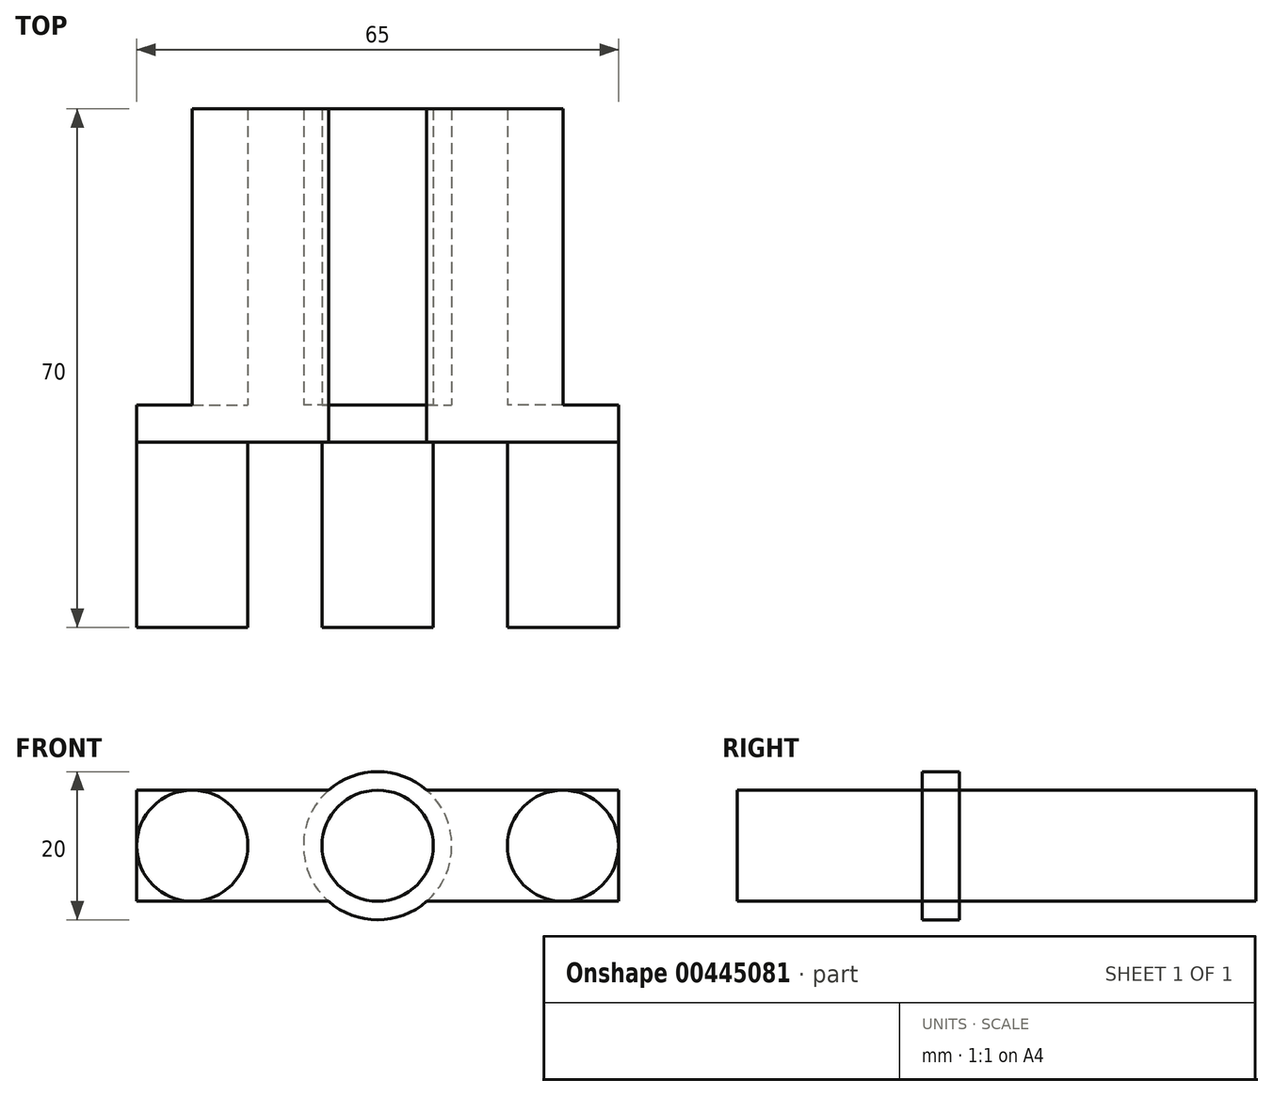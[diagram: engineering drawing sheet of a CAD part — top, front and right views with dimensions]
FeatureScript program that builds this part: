
annotation { "Feature Type Name" : "Feature", "Feature Type Description" : "" }
export const myFeature = defineFeature(function(context is Context, id is Id, definition is map)
    precondition{}
    {
        {
            var Q0;
            Q0=qCreatedBy(makeId("Front.planeOp"),FACE);
            var sketch = newSketch(context, id + "F0", { "sketchPlane" : qUnion([Q0])});
            skLineSegment(sketch, "E0.bottom", {"start": v(-32.5, 7.5) * mm, "end": v(32.5, 7.5) * mm});
            skLineSegment(sketch, "E0.top", {"start": v(-32.5, -7.5) * mm, "end": v(32.5, -7.5) * mm});
            skLineSegment(sketch, "E0.left", {"start": v(-32.5, 7.5) * mm, "end": v(-32.5, -7.5) * mm});
            skLineSegment(sketch, "E0.right", {"start": v(32.5, 7.5) * mm, "end": v(32.5, -7.5) * mm});
            skPoint(sketch, "E0.middle", {"position": v(0, 0) * mm});
            skCircle(sketch, "E1", {"center": v(0, 0) * mm, "radius": 7.5 * mm});
            skCircle(sketch, "E2", {"center": v(-25, 0) * mm, "radius": 7.5 * mm});
            skCircle(sketch, "E3", {"center": v(25, 0) * mm, "radius": 7.5 * mm});
            skCircle(sketch, "E4", {"center": v(0, 0) * mm, "radius": 10 * mm});
            skSolve(sketch);
        }
        {
            var Q0;
            Q0 = qSketchRegion(id + "F0", true);
            extrude(context, id + "F1", {"entities" : qUnion([Q0]), "depth" : 5 * mm});
        }
        {
            var Q0;
            {var subQ0=sQuery(id+"F0.wireOp",EDGE,"E1");var subQ1=makeQuery(id+"F0.imprint","INTERSECT",VERTEX,{"derivedFrom":[sQuery(id+"F0.wireOp",EDGE,"E0.bottom"),subQ0]});Q0=makeQuery(id+"F0.imprint","IMPRINT",FACE,{"disambiguationData":[TD([[makeQuery(id+"F0.imprint","IMPRINT",EDGE,{"disambiguationData":[TD([[subQ1,-1.0]])],"derivedFrom":subQ0}),1.0]])]});}
            var Q1;
            {var subQ0=sQuery(id+"F0.wireOp",EDGE,"E3");var subQ1=makeQuery(id+"F0.imprint","INTERSECT",VERTEX,{"derivedFrom":[sQuery(id+"F0.wireOp",EDGE,"E0.bottom"),subQ0]});Q1=makeQuery(id+"F0.imprint","IMPRINT",FACE,{"disambiguationData":[TD([[makeQuery(id+"F0.imprint","IMPRINT",EDGE,{"disambiguationData":[TD([[subQ1,1.0]])],"derivedFrom":subQ0}),1.0]])]});}
            var Q2;
            {var subQ0=sQuery(id+"F0.wireOp",EDGE,"E2");var subQ1=makeQuery(id+"F0.imprint","INTERSECT",VERTEX,{"derivedFrom":[sQuery(id+"F0.wireOp",EDGE,"E0.bottom"),subQ0]});Q2=makeQuery(id+"F0.imprint","IMPRINT",FACE,{"disambiguationData":[TD([[makeQuery(id+"F0.imprint","IMPRINT",EDGE,{"disambiguationData":[TD([[subQ1,-1.0]])],"derivedFrom":subQ0}),1.0]])]});}
            extrude(context, id + "F2", {"entities" : qUnion([Q0, Q1, Q2]), "operationType" : NewBodyOperationType.ADD, "depth" : 30 * mm});
        }
        {
            var Q0;
            {var subQ0=sQuery(id+"F0.wireOp",EDGE,"E4");var subQ1=sQuery(id+"F0.wireOp",EDGE,"E0.bottom");var subQ2=makeQuery(id+"F0.imprint","INTERSECT",VERTEX,{"disambiguationData":[OD(0.0)],"derivedFrom":[subQ1,subQ0]});Q0=makeQuery(id+"F0.imprint","IMPRINT",FACE,{"disambiguationData":[TD([[makeQuery(id+"F0.imprint","IMPRINT",EDGE,{"disambiguationData":[TD([[subQ2,-1.0]])],"derivedFrom":subQ1}),-1.0]])]});}
            var Q1;
            {var subQ0=sQuery(id+"F0.wireOp",EDGE,"E1");var subQ1=makeQuery(id+"F0.imprint","INTERSECT",VERTEX,{"derivedFrom":[sQuery(id+"F0.wireOp",EDGE,"E0.bottom"),subQ0]});Q1=makeQuery(id+"F0.imprint","IMPRINT",FACE,{"disambiguationData":[TD([[makeQuery(id+"F0.imprint","IMPRINT",EDGE,{"disambiguationData":[TD([[subQ1,-1.0]])],"derivedFrom":subQ0}),1.0]])]});}
            var Q2;
            {var subQ0=sQuery(id+"F0.wireOp",EDGE,"E4");var subQ1=sQuery(id+"F0.wireOp",EDGE,"E0.top");var subQ2=makeQuery(id+"F0.imprint","INTERSECT",VERTEX,{"disambiguationData":[OD(0.0)],"derivedFrom":[subQ1,subQ0]});Q2=makeQuery(id+"F0.imprint","IMPRINT",FACE,{"disambiguationData":[TD([[makeQuery(id+"F0.imprint","IMPRINT",EDGE,{"disambiguationData":[TD([[subQ2,-1.0]])],"derivedFrom":subQ1}),-1.0]])]});}
            var Q3;
            {var subQ0=sQuery(id+"F0.wireOp",EDGE,"E4");var subQ1=sQuery(id+"F0.wireOp",EDGE,"E0.bottom");var subQ2=makeQuery(id+"F0.imprint","INTERSECT",VERTEX,{"disambiguationData":[OD(1.0)],"derivedFrom":[subQ1,subQ0]});Q3=makeQuery(id+"F0.imprint","IMPRINT",FACE,{"disambiguationData":[TD([[makeQuery(id+"F0.imprint","IMPRINT",EDGE,{"disambiguationData":[TD([[subQ2,1.0]])],"derivedFrom":subQ1}),-1.0]])]});}
            var Q4;
            {var subQ0=sQuery(id+"F0.wireOp",EDGE,"E4");var subQ1=sQuery(id+"F0.wireOp",EDGE,"E0.bottom");var subQ2=makeQuery(id+"F0.imprint","INTERSECT",VERTEX,{"disambiguationData":[OD(0.0)],"derivedFrom":[subQ1,subQ0]});Q4=makeQuery(id+"F0.imprint","IMPRINT",FACE,{"disambiguationData":[TD([[makeQuery(id+"F0.imprint","IMPRINT",EDGE,{"disambiguationData":[TD([[subQ2,-1.0]])],"derivedFrom":subQ1}),1.0]])]});}
            extrude(context, id + "F3", {"entities" : qUnion([Q0, Q1, Q2, Q3, Q4]), "operationType" : NewBodyOperationType.ADD, "oppositeDirection" : true, "depth" : 40 * mm});
        }
    });
